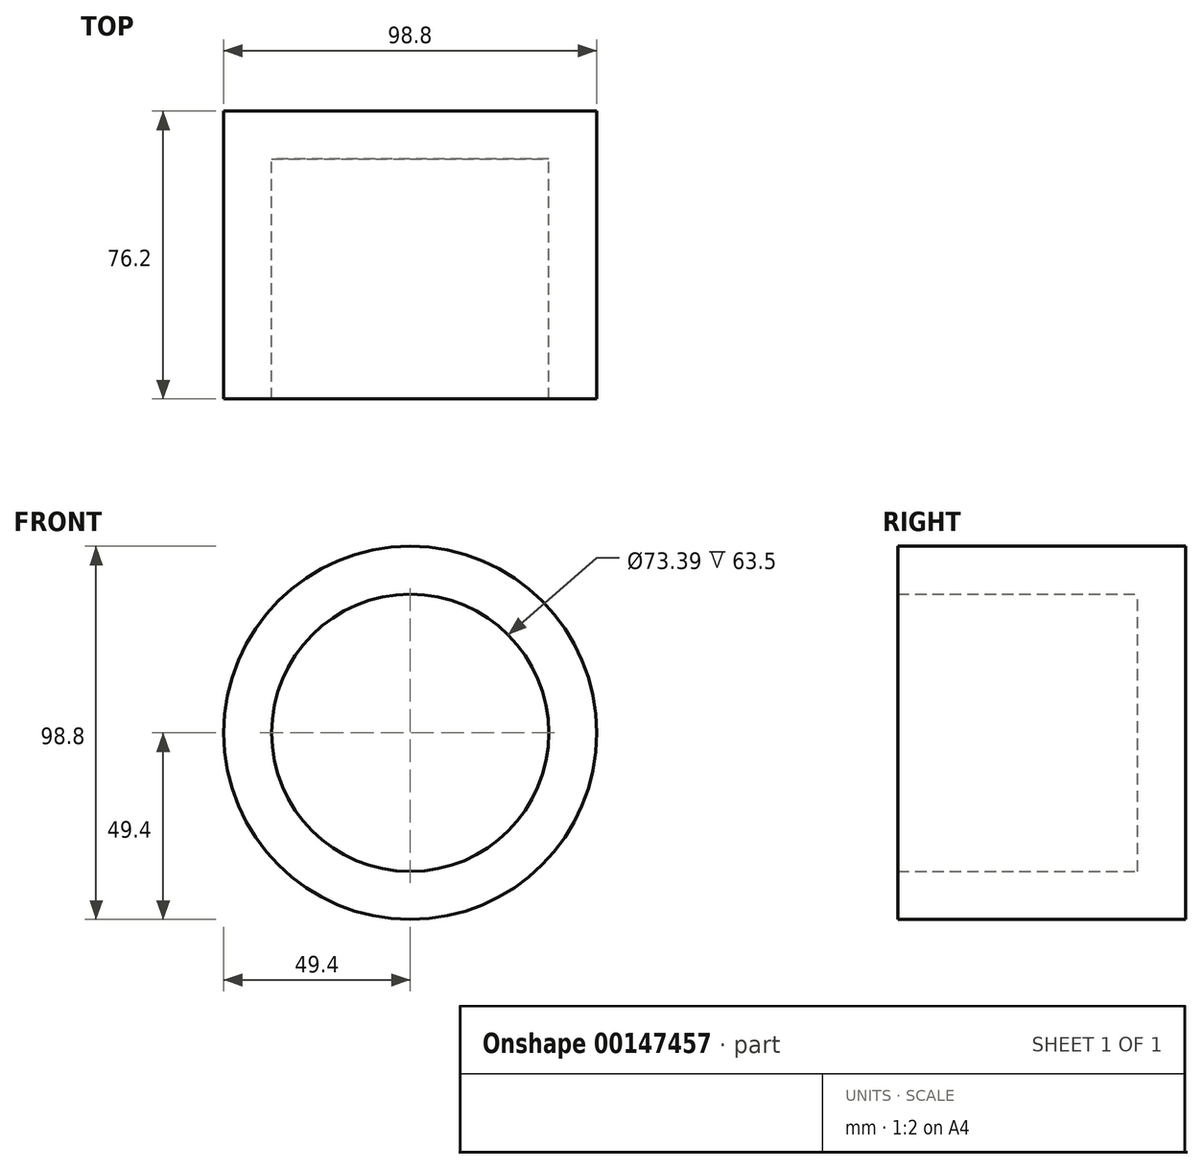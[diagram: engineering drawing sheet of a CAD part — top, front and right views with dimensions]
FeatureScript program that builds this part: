
annotation { "Feature Type Name" : "Feature", "Feature Type Description" : "" }
export const myFeature = defineFeature(function(context is Context, id is Id, definition is map)
    precondition{}
    {
        {
            var Q0;
            Q0=qCreatedBy(makeId("Front.planeOp"),FACE);
            var sketch = newSketch(context, id + "F0", { "sketchPlane" : qUnion([Q0])});
            skCircle(sketch, "E0", {"center": v(0, 0) * mm, "radius": 49.4 * mm});
            skSolve(sketch);
        }
        {
            var Q0;
            Q0=makeQuery(id+"F0.imprint","IMPRINT",FACE,{"disambiguationData":[TD([[makeQuery(id+"F0.imprint","IMPRINT",EDGE,{"derivedFrom":sQuery(id+"F0.wireOp",EDGE,"E0")}),1.0]])]});
            extrude(context, id + "F1", {"entities" : qUnion([Q0]), "depth" : 76.2 * mm});
        }
        {
            var Q0;
            Q0=qCreatedBy(makeId("Front.planeOp"),FACE);
            var sketch = newSketch(context, id + "F2", { "sketchPlane" : qUnion([Q0])});
            skCircle(sketch, "E1", {"center": v(0, 0) * mm, "radius": 23.86 * mm});
            skSolve(sketch);
        }
        {
            var Q0;
            Q0=makeQuery(id+"F2.imprint","IMPRINT",FACE,{"disambiguationData":[TD([[makeQuery(id+"F2.imprint","IMPRINT",EDGE,{"derivedFrom":sQuery(id+"F2.wireOp",EDGE,"E1")}),1.0]])]});
            extrude(context, id + "F3", {"entities" : qUnion([Q0]), "operationType" : NewBodyOperationType.ADD, "depth" : 50.8 * mm});
        }
        {
            var Q0;
            Q0=makeQuery(id+"F1.opExtrude","CAP_FACE",FACE,{"disambiguationData":[OSD([sQuery(id+"F0.wireOp",EDGE,"E0")])],"isStart":false});
            shell(context, id + "F4", {"entities" : qUnion([Q0]), "thickness" : 12.7 * mm});
        }
    });
